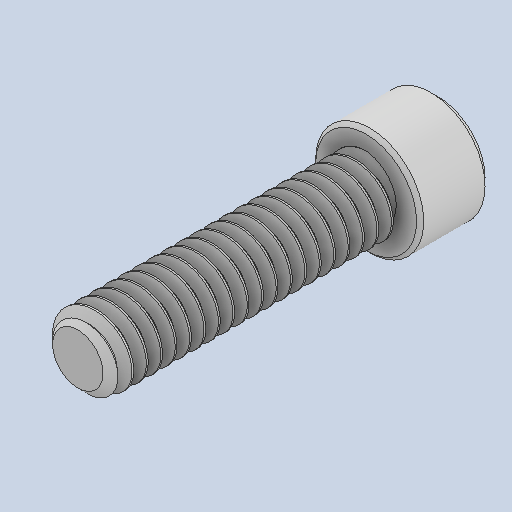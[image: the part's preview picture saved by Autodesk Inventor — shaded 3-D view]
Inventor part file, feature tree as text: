
AUTODESK INVENTOR PART (.ipt)
format: ipt  version: 2022.3 (Build 263350000, 350)  size: 753,152 bytes
history: native  units: in
note: dims shown in document units (in); Inventor stores cm internally (conversion verified against a paired STEP export)
features: chamfer x1
ambient origin geometry x8: Origin, YZ Plane, XZ Plane, XY Plane, X Axis, Y Axis, Z Axis, Center Point
bodies: Solid1 (feature_tree)
feature tree (1):
  chamfer  "Chamfer2"  [1 undecoded]
note: 1 required parameter value undecoded (feature->parameter linkage not recoverable at this tier; creation-order binding heuristic only, values carry confidence <= 0.55)
